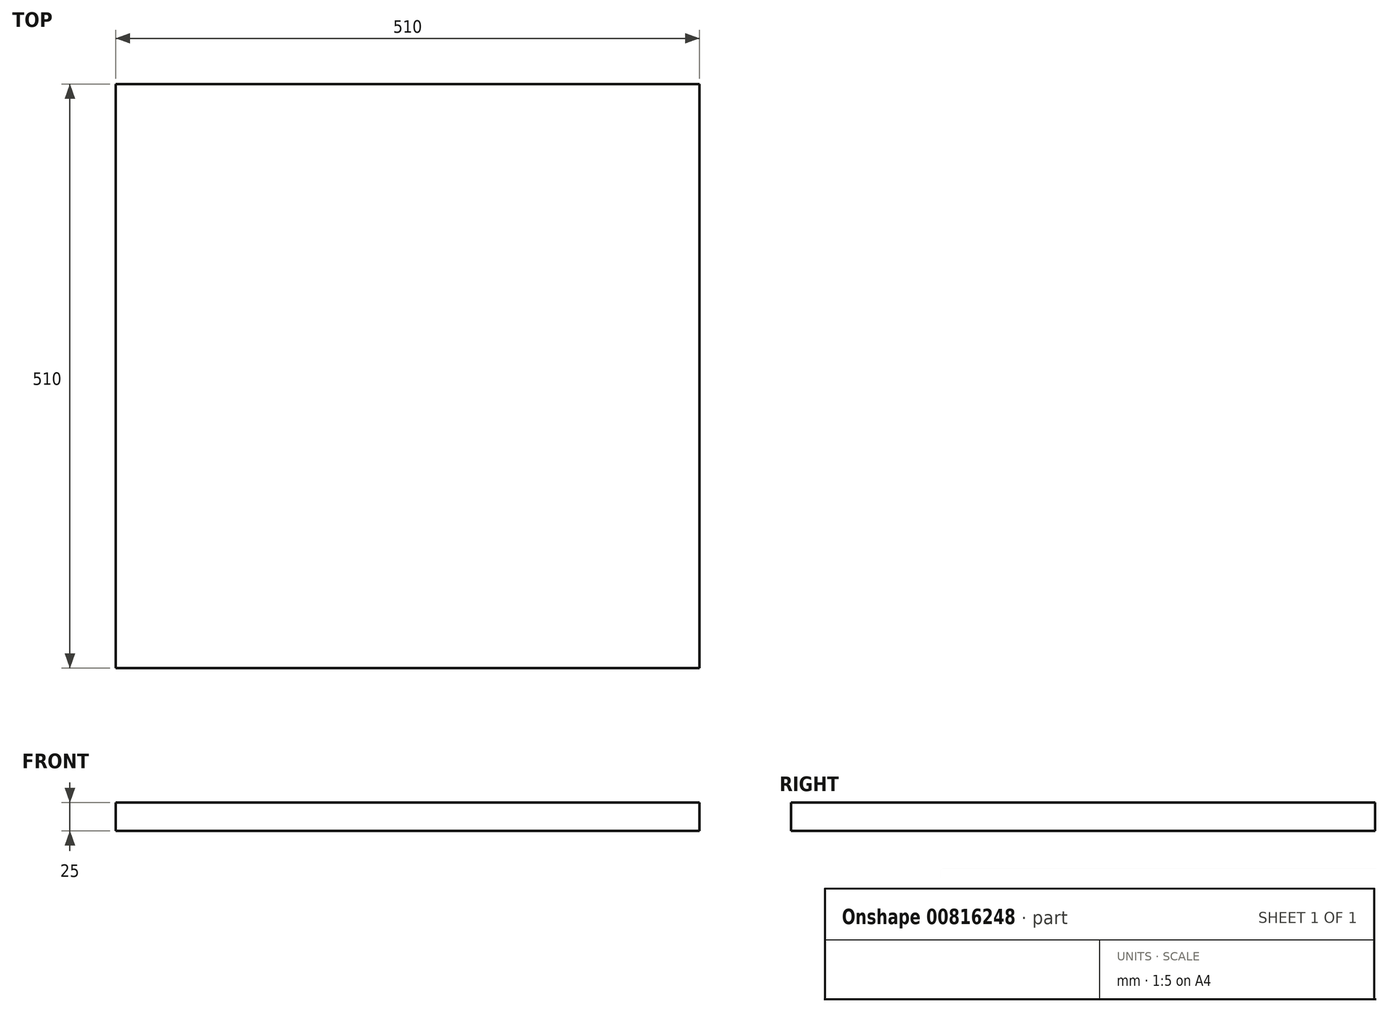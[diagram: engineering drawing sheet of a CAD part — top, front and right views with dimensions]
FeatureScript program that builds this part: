
annotation { "Feature Type Name" : "Feature", "Feature Type Description" : "" }
export const myFeature = defineFeature(function(context is Context, id is Id, definition is map)
    precondition{}
    {
        {
            var Q0;
            Q0=qCreatedBy(makeId("Top.planeOp"),FACE);
            var sketch = newSketch(context, id + "F0", { "sketchPlane" : qUnion([Q0])});
            skLineSegment(sketch, "E0.bottom", {"start": v(0, 0) * mm, "end": v(500, 0) * mm, "construction": true});
            skLineSegment(sketch, "E0.top", {"start": v(0, 500) * mm, "end": v(500, 500) * mm, "construction": true});
            skLineSegment(sketch, "E0.left", {"start": v(0, 0) * mm, "end": v(0, 500) * mm, "construction": true});
            skLineSegment(sketch, "E0.right", {"start": v(500, 0) * mm, "end": v(500, 500) * mm, "construction": true});
            skLineSegment(sketch, "E1.0", {"start": v(-5, -5) * mm, "end": v(505, -5) * mm});
            skLineSegment(sketch, "E1.1", {"start": v(-5, -5) * mm, "end": v(-5, 505) * mm});
            skLineSegment(sketch, "E1.2", {"start": v(-5, 505) * mm, "end": v(505, 505) * mm});
            skLineSegment(sketch, "E1.3", {"start": v(505, -5) * mm, "end": v(505, 505) * mm});
            skSolve(sketch);
        }
        {
            var Q0;
            Q0 = qSketchRegion(id + "F0", true);
            extrude(context, id + "F1", {"entities" : qUnion([Q0]), "depth" : 25 * mm, "offsetDistance" : 25 * mm});
        }
    });
